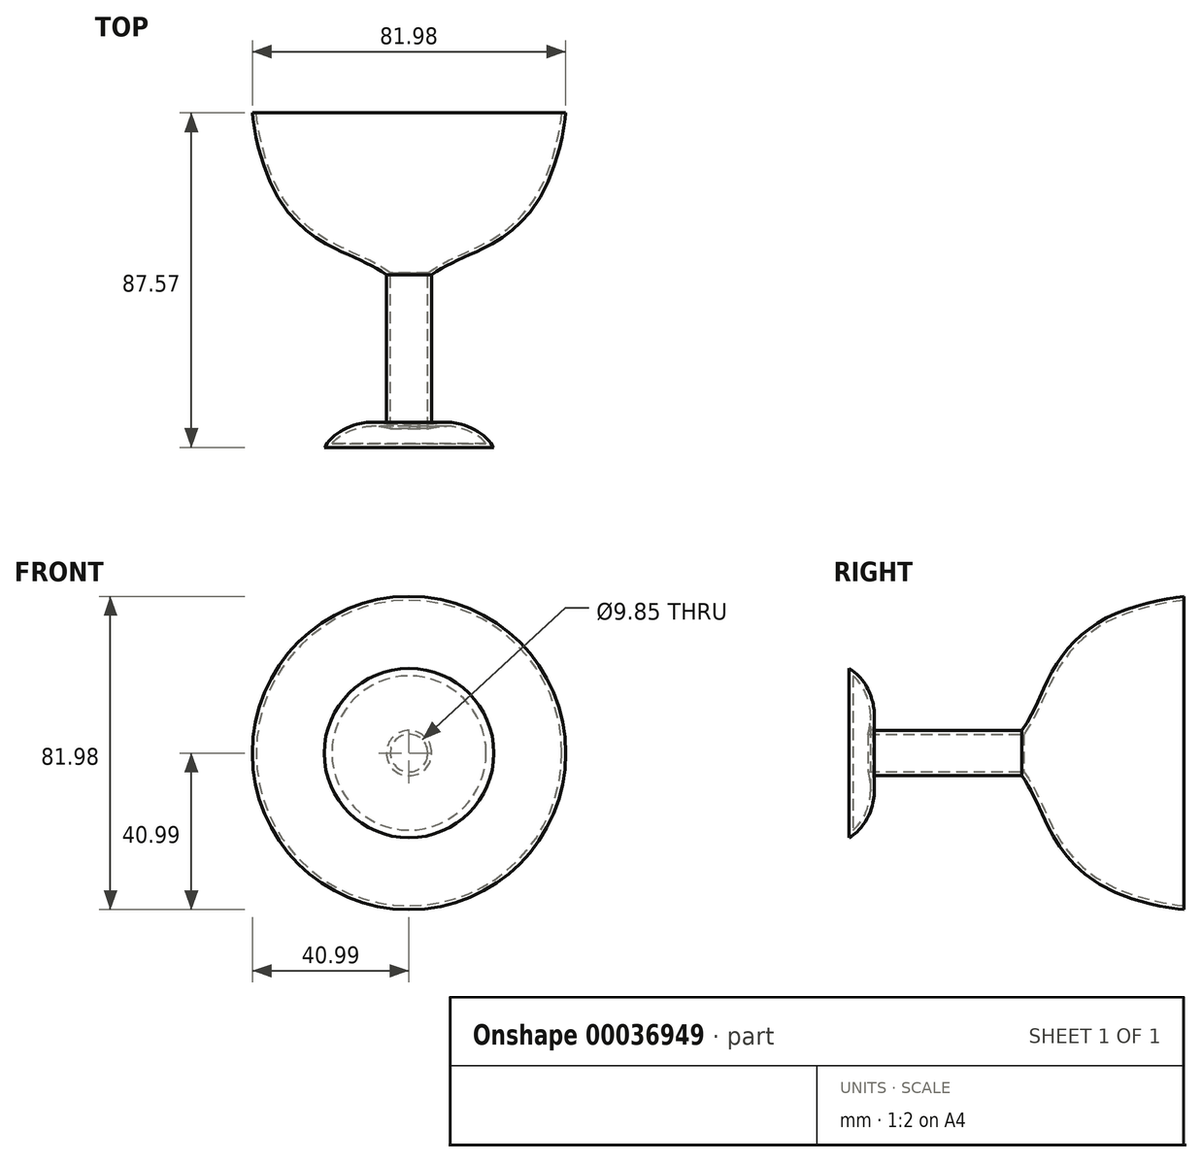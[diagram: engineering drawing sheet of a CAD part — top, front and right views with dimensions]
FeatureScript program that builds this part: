
annotation { "Feature Type Name" : "Feature", "Feature Type Description" : "" }
export const myFeature = defineFeature(function(context is Context, id is Id, definition is map)
    precondition{}
    {
        {
            var Q0;
            Q0=qCreatedBy(makeId("Top.planeOp"),FACE);
            var sketch = newSketch(context, id + "F0", { "sketchPlane" : qUnion([Q0])});
            skLineSegment(sketch, "E0", {"start": v(0, 41.7) * mm, "end": v(0, -45.88) * mm});
            skLineSegment(sketch, "E1", {"start": v(40.99, 41.7) * mm, "end": v(0, 41.7) * mm});
            skLineSegment(sketch, "E2", {"start": v(22.17, -45.88) * mm, "end": v(0, -45.88) * mm});
            skLineSegment(sketch, "E3", {"start": v(5.92, -0.7) * mm, "end": v(5.92, -39.73) * mm});
            skFitSpline(sketch, "E4", {"points": [v(40.99, 41.7) * mm, v(35.37, 21.48) * mm, v(22.18, 7.72) * mm, v(5.92, -0.7) * mm], "startDerivative": vector(-4.26, -44.89) * mm, "endDerivative": vector(-45.63, -32.17) * mm});
            skFitSpline(sketch, "E5", {"points": [v(5.92, -39.73) * mm, v(13.2, -39.73) * mm, v(22.17, -45.88) * mm], "startDerivative": vector(19.94, 3.88) * mm, "endDerivative": vector(13.4, -21.15) * mm});
            skSolve(sketch);
        }
        {
            var Q0;
            Q0=makeQuery(id+"F0.imprint","IMPRINT",FACE,{"disambiguationData":[TD([[makeQuery(id+"F0.imprint","IMPRINT",EDGE,{"derivedFrom":sQuery(id+"F0.wireOp",EDGE,"E0")}),1.0]])]});
            var Q1;
            Q1=sQuery(id+"F0.wireOp",EDGE,"E0");
            revolve(context, id + "F1", {"entities" : qUnion([Q0]), "axis" : qUnion([Q1]), "revolveType" : RevolveType.FULL});
        }
        {
            var Q0;
            Q0=makeQuery(id+"F1.opRevolve","SWEPT_FACE",FACE,{"disambiguationData":[OSD([sQuery(id+"F0.wireOp",EDGE,"E1")])]});
            shell(context, id + "F2", {"entities" : qUnion([Q0]), "thickness" : 1 * mm});
        }
    });
